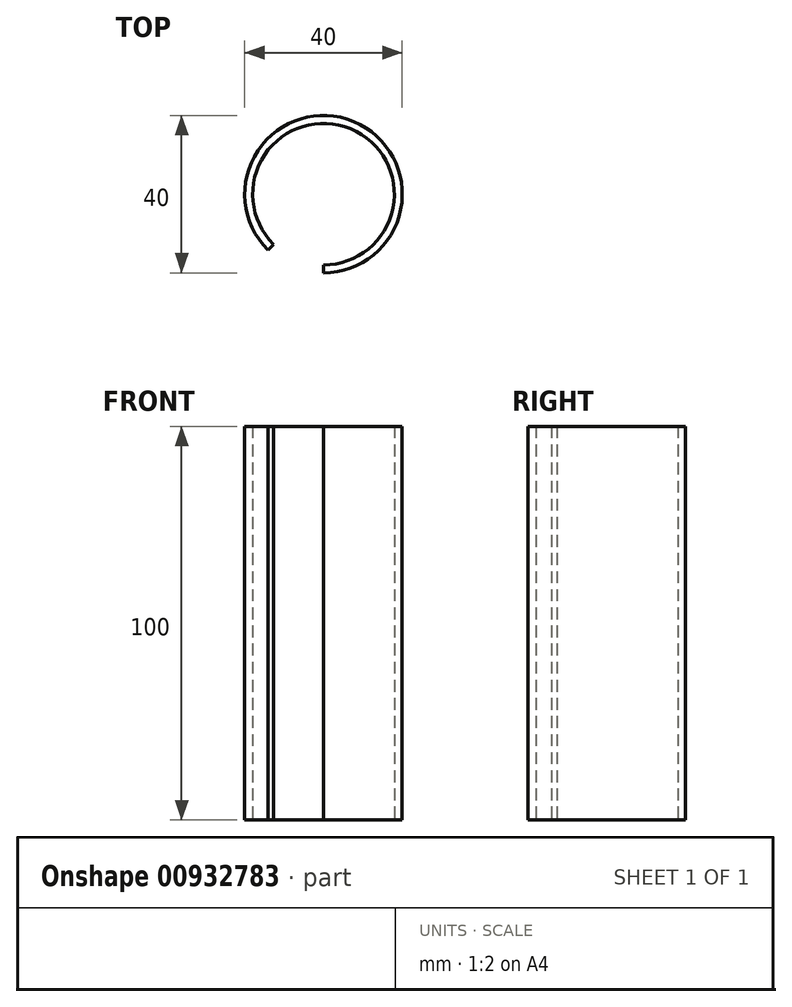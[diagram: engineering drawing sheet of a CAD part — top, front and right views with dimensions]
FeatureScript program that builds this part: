
annotation { "Feature Type Name" : "Feature", "Feature Type Description" : "" }
export const myFeature = defineFeature(function(context is Context, id is Id, definition is map)
    precondition{}
    {
        {
            var Q0;
            Q0=qCreatedBy(makeId("Top.planeOp"),FACE);
            var sketch = newSketch(context, id + "F0", { "sketchPlane" : qUnion([Q0])});
            skCircle(sketch, "E0", {"center": v(0, 0) * mm, "radius": 18 * mm});
            skCircle(sketch, "E1", {"center": v(0, 0) * mm, "radius": 20 * mm});
            skLineSegment(sketch, "E2", {"start": v(0, 0) * mm, "end": v(-14.14, -14.14) * mm});
            skLineSegment(sketch, "E3", {"start": v(0, 0) * mm, "end": v(0, -20) * mm});
            skSolve(sketch);
        }
        {
            var Q0;
            {var subQ0=sQuery(id+"F0.wireOp",EDGE,"E2");var subQ1=sQuery(id+"F0.wireOp",EDGE,"E0");var subQ2=makeQuery(id+"F0.imprint","INTERSECT",VERTEX,{"derivedFrom":[subQ1,subQ0]});Q0=makeQuery(id+"F0.imprint","IMPRINT",FACE,{"disambiguationData":[TD([[makeQuery(id+"F0.imprint","IMPRINT",EDGE,{"disambiguationData":[TD([[subQ2,1.0]])],"derivedFrom":subQ1}),-1.0]])]});}
            extrude(context, id + "F1", {"entities" : qUnion([Q0]), "depth" : 100 * mm, "offsetDistance" : 25 * mm});
        }
    });
